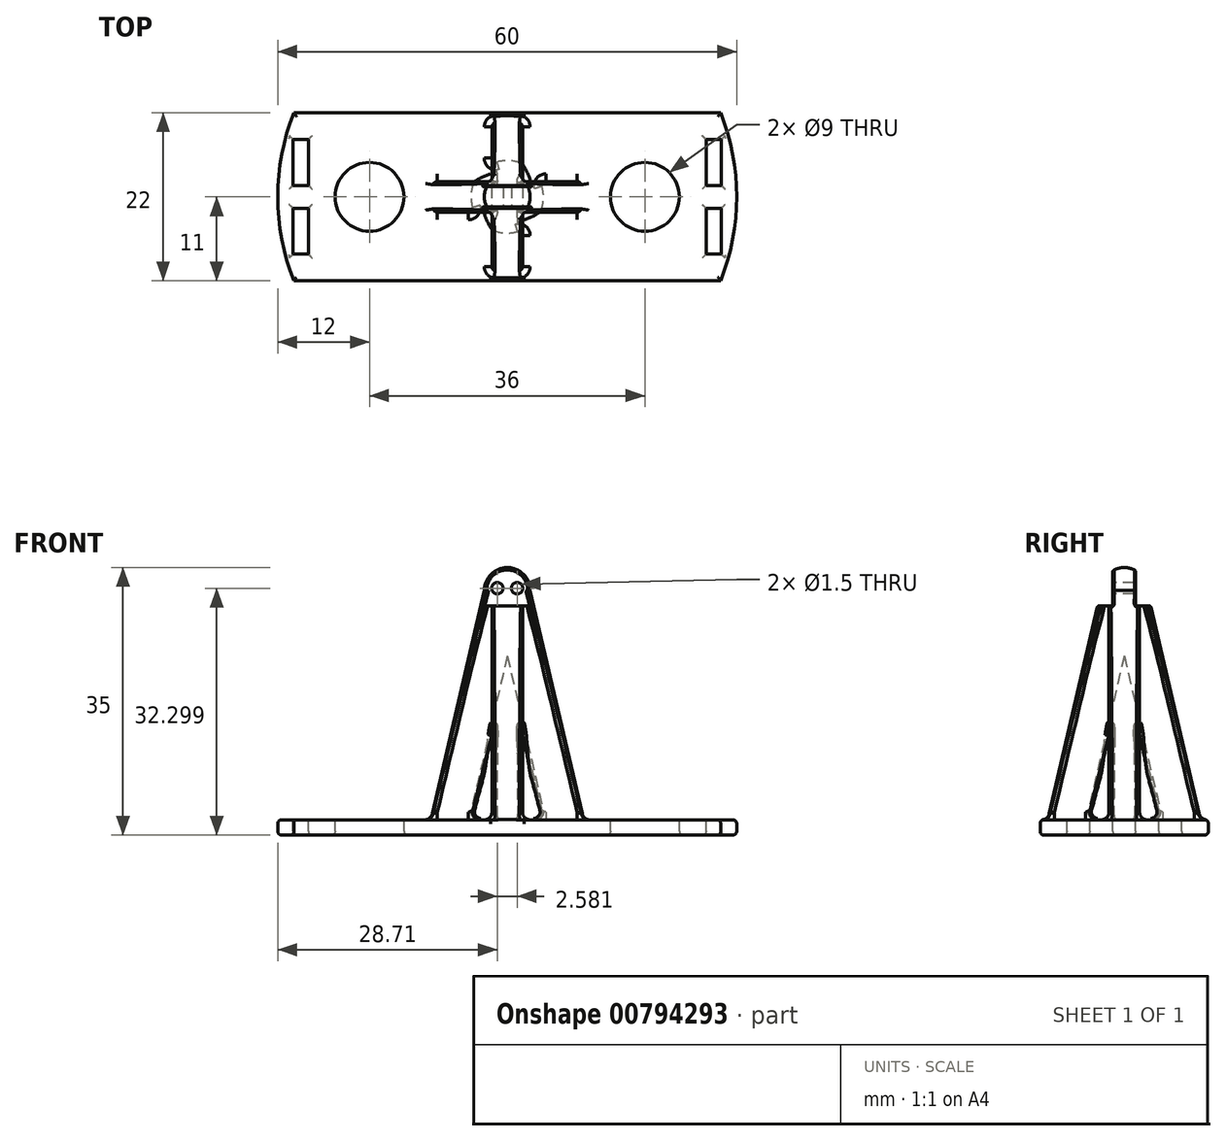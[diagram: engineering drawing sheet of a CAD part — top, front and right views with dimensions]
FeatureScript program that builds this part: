
annotation { "Feature Type Name" : "Feature", "Feature Type Description" : "" }
export const myFeature = defineFeature(function(context is Context, id is Id, definition is map)
    precondition{}
    {
        {
            var Q0;
            Q0=qCreatedBy(makeId("Front.planeOp"),FACE);
            var sketch = newSketch(context, id + "F0", { "sketchPlane" : qUnion([Q0])});
            skLineSegment(sketch, "E0", {"start": v(0, 0) * mm, "end": v(30, 0) * mm});
            skLineSegment(sketch, "E1", {"start": v(30, 0) * mm, "end": v(30, 2) * mm});
            skLineSegment(sketch, "E2", {"start": v(30, 2) * mm, "end": v(10, 2) * mm});
            skLineSegment(sketch, "E3", {"start": v(10, 2) * mm, "end": v(3, 32) * mm});
            skArc(sketch, "E4", {"start": v(3, 32) * mm, "mid": v(2.12, 34.12) * mm, "end": v(0, 35) * mm});
            skLineSegment(sketch, "E5", {"start": v(0, 32) * mm, "end": v(0, 35) * mm});
            skLineSegment(sketch, "E6", {"start": v(0, 2) * mm, "end": v(5, 2) * mm});
            skLineSegment(sketch, "E7", {"start": v(5, 2) * mm, "end": v(0, 23.43) * mm});
            skLineSegment(sketch, "E8", {"start": v(0, 32) * mm, "end": v(0, 23.43) * mm});
            skLineSegment(sketch, "E9", {"start": v(0, 2) * mm, "end": v(0, 0) * mm});
            skSolve(sketch);
        }
        {
            var Q0;
            Q0=makeQuery(id+"F0.imprint","IMPRINT",FACE,{"disambiguationData":[TD([[makeQuery(id+"F0.imprint","IMPRINT",EDGE,{"derivedFrom":sQuery(id+"F0.wireOp",EDGE,"E0")}),1.0]])]});
            var Q1;
            Q1=sQuery(id+"F0.wireOp",EDGE,"E8");
            revolve(context, id + "F1", {"surfaceOperationType" : NewSurfaceOperationType.NEW, "entities" : qUnion([Q0]), "axis" : qUnion([Q1]), "revolveType" : RevolveType.FULL});
        }
        {
            var Q0;
            Q0=makeQuery(id+"F1.opRevolve","SWEPT_FACE",FACE,{"disambiguationData":[OSD([sQuery(id+"F0.wireOp",EDGE,"E0")])]});
            var sketch = newSketch(context, id + "F2", { "sketchPlane" : qUnion([Q0])});
            skLineSegment(sketch, "E10.bottom", {"start": v(38.46, -11) * mm, "end": v(-38.46, -11) * mm});
            skLineSegment(sketch, "E10.top", {"start": v(38.46, 11) * mm, "end": v(-38.46, 11) * mm});
            skLineSegment(sketch, "E10.left", {"start": v(38.46, -11) * mm, "end": v(38.46, 11) * mm});
            skLineSegment(sketch, "E10.right", {"start": v(-38.46, -11) * mm, "end": v(-38.46, 11) * mm});
            skPoint(sketch, "E10.middle", {"position": v(0, 0) * mm});
            skSolve(sketch);
        }
        {
            var Q0;
            Q0 = qSketchRegion(id + "F2", true);
            extrude(context, id + "F3", {"entities" : qUnion([Q0]), "operationType" : NewBodyOperationType.INTERSECT, "endBound" : BoundingType.THROUGH_ALL, "oppositeDirection" : true, "depth" : 25 * mm, "offsetDistance" : 25 * mm});
        }
        {
            var Q0;
            Q0=makeQuery(id+"F3.boolean.opBoolean","SPLIT",FACE,{"disambiguationData":[OD(0.0)],"derivedFrom":makeQuery(id+"F1.opRevolve","SWEPT_FACE",FACE,{"disambiguationData":[OSD([sQuery(id+"F0.wireOp",EDGE,"E2")])]})});
            var sketch = newSketch(context, id + "F4", { "sketchPlane" : qUnion([Q0])});
            skLineSegment(sketch, "E11.bottom", {"start": v(-2, 2) * mm, "end": v(-12, 2) * mm});
            skLineSegment(sketch, "E11.top", {"start": v(-2, 12) * mm, "end": v(-12, 12) * mm});
            skLineSegment(sketch, "E11.left", {"start": v(-2, 2) * mm, "end": v(-2, 12) * mm});
            skLineSegment(sketch, "E11.right", {"start": v(-12, 2) * mm, "end": v(-12, 12) * mm});
            skLineSegment(sketch, "E12.1.0", {"start": v(-2, -2) * mm, "end": v(-2, -12) * mm});
            skLineSegment(sketch, "E12.1.1", {"start": v(-2, -2) * mm, "end": v(-12, -2) * mm});
            skLineSegment(sketch, "E12.1.2", {"start": v(-12, -2) * mm, "end": v(-12, -12) * mm});
            skLineSegment(sketch, "E12.1.3", {"start": v(-2, -12) * mm, "end": v(-12, -12) * mm});
            skLineSegment(sketch, "E12.2.0", {"start": v(2, -2) * mm, "end": v(12, -2) * mm});
            skLineSegment(sketch, "E12.2.1", {"start": v(2, -2) * mm, "end": v(2, -12) * mm});
            skLineSegment(sketch, "E12.2.2", {"start": v(2, -12) * mm, "end": v(12, -12) * mm});
            skLineSegment(sketch, "E12.2.3", {"start": v(12, -2) * mm, "end": v(12, -12) * mm});
            skLineSegment(sketch, "E12.3.0", {"start": v(2, 2) * mm, "end": v(2, 12) * mm});
            skLineSegment(sketch, "E12.3.1", {"start": v(2, 2) * mm, "end": v(12, 2) * mm});
            skLineSegment(sketch, "E12.3.2", {"start": v(12, 2) * mm, "end": v(12, 12) * mm});
            skLineSegment(sketch, "E12.3.3", {"start": v(2, 12) * mm, "end": v(12, 12) * mm});
            skPoint(sketch, "E12.center", {"position": v(0, 0) * mm});
            skSolve(sketch);
        }
        {
            var Q0;
            Q0 = qSketchRegion(id + "F4", true);
            extrude(context, id + "F5", {"entities" : qUnion([Q0]), "operationType" : NewBodyOperationType.REMOVE, "endBound" : BoundingType.THROUGH_ALL, "depth" : 25 * mm, "offsetDistance" : 25 * mm});
        }
        {
            var Q0;
            {var subQ0=makeQuery(id+"F1.opRevolve","SWEPT_FACE",FACE,{"disambiguationData":[OSD([sQuery(id+"F0.wireOp",EDGE,"E2")])]});Q0=makeQuery(id+"F5.boolean.opBoolean","MERGE",FACE,{"derivedFrom":[makeQuery(id+"F1.opRevolve","SWEPT_FACE",FACE,{"disambiguationData":[OSD([sQuery(id+"F0.wireOp",EDGE,"E6")])]}),makeQuery(id+"F3.boolean.opBoolean","SPLIT",FACE,{"disambiguationData":[OD(0.0)],"derivedFrom":subQ0}),makeQuery(id+"F3.boolean.opBoolean","SPLIT",FACE,{"disambiguationData":[OD(1.0)],"derivedFrom":subQ0}),makeQuery(id+"F5.opExtrude","CAP_FACE",FACE,{"disambiguationData":[OSD([sQuery(id+"F4.wireOp",EDGE,"E11.bottom"),sQuery(id+"F4.wireOp",EDGE,"E11.top"),sQuery(id+"F4.wireOp",EDGE,"E11.left"),sQuery(id+"F4.wireOp",EDGE,"E11.right")])],"isStart":true}),makeQuery(id+"F5.opExtrude","CAP_FACE",FACE,{"disambiguationData":[OSD([sQuery(id+"F4.wireOp",EDGE,"E12.1.0"),sQuery(id+"F4.wireOp",EDGE,"E12.1.1"),sQuery(id+"F4.wireOp",EDGE,"E12.1.2"),sQuery(id+"F4.wireOp",EDGE,"E12.1.3")])],"isStart":true}),makeQuery(id+"F5.opExtrude","CAP_FACE",FACE,{"disambiguationData":[OSD([sQuery(id+"F4.wireOp",EDGE,"E12.2.0"),sQuery(id+"F4.wireOp",EDGE,"E12.2.1"),sQuery(id+"F4.wireOp",EDGE,"E12.2.2"),sQuery(id+"F4.wireOp",EDGE,"E12.2.3")])],"isStart":true}),makeQuery(id+"F5.opExtrude","CAP_FACE",FACE,{"disambiguationData":[OSD([sQuery(id+"F4.wireOp",EDGE,"E12.3.0"),sQuery(id+"F4.wireOp",EDGE,"E12.3.1"),sQuery(id+"F4.wireOp",EDGE,"E12.3.2"),sQuery(id+"F4.wireOp",EDGE,"E12.3.3")])],"isStart":true})]});}
            cPlane(context, id + "F6", {"entities" : qUnion([Q0]), "cplaneType" : CPlaneType.OFFSET, "offset" : 33 * mm, "width" : 150 * mm, "height" : 150 * mm});
        }
        {
            var Q0;
            Q0=qCreatedBy(id+"F6.planeOp",FACE);
            var sketch = newSketch(context, id + "F7", { "sketchPlane" : qUnion([Q0])});
            skLineSegment(sketch, "E13.bottom", {"start": v(5, 1.5) * mm, "end": v(-5, 1.5) * mm, "construction": true});
            skLineSegment(sketch, "E13.top", {"start": v(5, -1.5) * mm, "end": v(-5, -1.5) * mm, "construction": true});
            skLineSegment(sketch, "E13.left", {"start": v(5, 1.5) * mm, "end": v(5, -1.5) * mm, "construction": true});
            skLineSegment(sketch, "E13.right", {"start": v(-5, 1.5) * mm, "end": v(-5, -1.5) * mm, "construction": true});
            skPoint(sketch, "E13.middle", {"position": v(0, 0) * mm});
            skLineSegment(sketch, "E14.bottom", {"start": v(-5, 1.5) * mm, "end": v(5, 1.5) * mm});
            skLineSegment(sketch, "E14.top", {"start": v(-5, 6.5) * mm, "end": v(5, 6.5) * mm});
            skLineSegment(sketch, "E14.left", {"start": v(-5, 1.5) * mm, "end": v(-5, 6.5) * mm});
            skLineSegment(sketch, "E14.right", {"start": v(5, 1.5) * mm, "end": v(5, 6.5) * mm});
            skLineSegment(sketch, "E15.bottom", {"start": v(-5, -1.5) * mm, "end": v(5, -1.5) * mm});
            skLineSegment(sketch, "E15.top", {"start": v(-5, -6.5) * mm, "end": v(5, -6.5) * mm});
            skLineSegment(sketch, "E15.left", {"start": v(-5, -1.5) * mm, "end": v(-5, -6.5) * mm});
            skLineSegment(sketch, "E15.right", {"start": v(5, -1.5) * mm, "end": v(5, -6.5) * mm});
            skSolve(sketch);
        }
        {
            var Q0;
            Q0 = qSketchRegion(id + "F7", true);
            extrude(context, id + "F8", {"entities" : qUnion([Q0]), "operationType" : NewBodyOperationType.REMOVE, "oppositeDirection" : true, "depth" : 5 * mm, "offsetDistance" : 25 * mm});
        }
        {
            var Q0;
            {var subQ0=makeQuery(id+"F1.opRevolve","SWEPT_FACE",FACE,{"disambiguationData":[OSD([sQuery(id+"F0.wireOp",EDGE,"E2")])]});Q0=makeQuery(id+"F5.boolean.opBoolean","MERGE",FACE,{"derivedFrom":[makeQuery(id+"F1.opRevolve","SWEPT_FACE",FACE,{"disambiguationData":[OSD([sQuery(id+"F0.wireOp",EDGE,"E6")])]}),makeQuery(id+"F3.boolean.opBoolean","SPLIT",FACE,{"disambiguationData":[OD(0.0)],"derivedFrom":subQ0}),makeQuery(id+"F3.boolean.opBoolean","SPLIT",FACE,{"disambiguationData":[OD(1.0)],"derivedFrom":subQ0}),makeQuery(id+"F5.opExtrude","CAP_FACE",FACE,{"disambiguationData":[OSD([sQuery(id+"F4.wireOp",EDGE,"E11.bottom"),sQuery(id+"F4.wireOp",EDGE,"E11.top"),sQuery(id+"F4.wireOp",EDGE,"E11.left"),sQuery(id+"F4.wireOp",EDGE,"E11.right")])],"isStart":true}),makeQuery(id+"F5.opExtrude","CAP_FACE",FACE,{"disambiguationData":[OSD([sQuery(id+"F4.wireOp",EDGE,"E12.1.0"),sQuery(id+"F4.wireOp",EDGE,"E12.1.1"),sQuery(id+"F4.wireOp",EDGE,"E12.1.2"),sQuery(id+"F4.wireOp",EDGE,"E12.1.3")])],"isStart":true}),makeQuery(id+"F5.opExtrude","CAP_FACE",FACE,{"disambiguationData":[OSD([sQuery(id+"F4.wireOp",EDGE,"E12.2.0"),sQuery(id+"F4.wireOp",EDGE,"E12.2.1"),sQuery(id+"F4.wireOp",EDGE,"E12.2.2"),sQuery(id+"F4.wireOp",EDGE,"E12.2.3")])],"isStart":true}),makeQuery(id+"F5.opExtrude","CAP_FACE",FACE,{"disambiguationData":[OSD([sQuery(id+"F4.wireOp",EDGE,"E12.3.0"),sQuery(id+"F4.wireOp",EDGE,"E12.3.1"),sQuery(id+"F4.wireOp",EDGE,"E12.3.2"),sQuery(id+"F4.wireOp",EDGE,"E12.3.3")])],"isStart":true})]});}
            var sketch = newSketch(context, id + "F9", { "sketchPlane" : qUnion([Q0])});
            skLineSegment(sketch, "E16", {"start": v(0, 0) * mm, "end": v(0, 11) * mm, "construction": true});
            skLineSegment(sketch, "E17", {"start": v(0, 0) * mm, "end": v(-30, 0) * mm, "construction": true});
            skLineSegment(sketch, "E18.bottom", {"start": v(-26, 1.5) * mm, "end": v(-28, 1.5) * mm});
            skLineSegment(sketch, "E18.top", {"start": v(-26, 7.5) * mm, "end": v(-28, 7.5) * mm});
            skLineSegment(sketch, "E18.left", {"start": v(-26, 1.5) * mm, "end": v(-26, 7.5) * mm});
            skLineSegment(sketch, "E18.right", {"start": v(-28, 1.5) * mm, "end": v(-28, 7.5) * mm});
            skLineSegment(sketch, "E19.MirrorCS", {"start": v(26, 1.5) * mm, "end": v(28, 1.5) * mm});
            skLineSegment(sketch, "E20.MirrorCS", {"start": v(26, 7.5) * mm, "end": v(28, 7.5) * mm});
            skLineSegment(sketch, "E21.MirrorCS", {"start": v(28, 1.5) * mm, "end": v(28, 7.5) * mm});
            skLineSegment(sketch, "E22.MirrorCS", {"start": v(26, 1.5) * mm, "end": v(26, 7.5) * mm});
            skLineSegment(sketch, "E23.MirrorCS", {"start": v(26, -7.5) * mm, "end": v(28, -7.5) * mm});
            skLineSegment(sketch, "E24.MirrorCS", {"start": v(28, -1.5) * mm, "end": v(28, -7.5) * mm});
            skLineSegment(sketch, "E25.MirrorCS", {"start": v(26, -1.5) * mm, "end": v(26, -7.5) * mm});
            skLineSegment(sketch, "E26.MirrorCS", {"start": v(26, -1.5) * mm, "end": v(28, -1.5) * mm});
            skLineSegment(sketch, "E27.MirrorCS", {"start": v(-28, -1.5) * mm, "end": v(-28, -7.5) * mm});
            skLineSegment(sketch, "E28.MirrorCS", {"start": v(-26, -1.5) * mm, "end": v(-26, -7.5) * mm});
            skLineSegment(sketch, "E29.MirrorCS", {"start": v(-26, -7.5) * mm, "end": v(-28, -7.5) * mm});
            skLineSegment(sketch, "E30.MirrorCS", {"start": v(-26, -1.5) * mm, "end": v(-28, -1.5) * mm});
            skSolve(sketch);
        }
        {
            var Q0;
            Q0 = qSketchRegion(id + "F9", true);
            extrude(context, id + "F10", {"entities" : qUnion([Q0]), "operationType" : NewBodyOperationType.REMOVE, "endBound" : BoundingType.UP_TO_NEXT, "oppositeDirection" : true, "depth" : 25 * mm, "offsetDistance" : 25 * mm});
        }
        {
            var Q0;
            Q0=makeQuery(id+"F8.boolean.opBoolean","COPY",FACE,{"derivedFrom":makeQuery(id+"F8.opExtrude","SWEPT_FACE",FACE,{"disambiguationData":[OSD([sQuery(id+"F7.wireOp",EDGE,"E15.bottom")])]})});
            var sketch = newSketch(context, id + "F11", { "sketchPlane" : qUnion([Q0])});
            skLineSegment(sketch, "E31", {"start": v(0, 34.6) * mm, "end": v(0, 30) * mm, "construction": true});
            skCircle(sketch, "E32", {"center": v(-1.3, 32.3) * mm, "radius": 0.75 * mm});
            skPoint(sketch, "E33", {"position": v(0, 32.3) * mm});
            skCircle(sketch, "E34.MirrorC", {"center": v(1.3, 32.3) * mm, "radius": 0.75 * mm});
            skLineSegment(sketch, "E35", {"start": v(0, 32.3) * mm, "end": v(-2.58, 32.3) * mm, "construction": true});
            skSolve(sketch);
        }
        {
            var Q0;
            Q0 = qSketchRegion(id + "F11", true);
            extrude(context, id + "F12", {"entities" : qUnion([Q0]), "operationType" : NewBodyOperationType.REMOVE, "endBound" : BoundingType.UP_TO_NEXT, "oppositeDirection" : true, "depth" : 25 * mm, "offsetDistance" : 25 * mm});
        }
        {
            var Q0;
            Q0=makeQuery(id+"F5.boolean.opBoolean","MERGE",FACE,{"derivedFrom":[makeQuery(id+"F1.opRevolve","SWEPT_FACE",FACE,{"disambiguationData":[OSD([sQuery(id+"F0.wireOp",EDGE,"E6")])]}),makeQuery(id+"F1.opRevolve","SWEPT_FACE",FACE,{"disambiguationData":[OSD([sQuery(id+"F0.wireOp",EDGE,"E2")])]}),makeQuery(id+"F5.opExtrude","CAP_FACE",FACE,{"disambiguationData":[OSD([sQuery(id+"F4.wireOp",EDGE,"E11.bottom"),sQuery(id+"F4.wireOp",EDGE,"E11.top"),sQuery(id+"F4.wireOp",EDGE,"E11.left"),sQuery(id+"F4.wireOp",EDGE,"E11.right")])],"isStart":true}),makeQuery(id+"F5.opExtrude","CAP_FACE",FACE,{"disambiguationData":[OSD([sQuery(id+"F4.wireOp",EDGE,"E12.1.0"),sQuery(id+"F4.wireOp",EDGE,"E12.1.1"),sQuery(id+"F4.wireOp",EDGE,"E12.1.2"),sQuery(id+"F4.wireOp",EDGE,"E12.1.3")])],"isStart":true}),makeQuery(id+"F5.opExtrude","CAP_FACE",FACE,{"disambiguationData":[OSD([sQuery(id+"F4.wireOp",EDGE,"E12.2.0"),sQuery(id+"F4.wireOp",EDGE,"E12.2.1"),sQuery(id+"F4.wireOp",EDGE,"E12.2.2"),sQuery(id+"F4.wireOp",EDGE,"E12.2.3")])],"isStart":true}),makeQuery(id+"F5.opExtrude","CAP_FACE",FACE,{"disambiguationData":[OSD([sQuery(id+"F4.wireOp",EDGE,"E12.3.0"),sQuery(id+"F4.wireOp",EDGE,"E12.3.1"),sQuery(id+"F4.wireOp",EDGE,"E12.3.2"),sQuery(id+"F4.wireOp",EDGE,"E12.3.3")])],"isStart":true})]});
            var sketch = newSketch(context, id + "F13", { "sketchPlane" : qUnion([Q0])});
            skCircle(sketch, "E36", {"center": v(-18, 0) * mm, "radius": 4.5 * mm});
            skLineSegment(sketch, "E37", {"start": v(0, 0) * mm, "end": v(0, 11) * mm, "construction": true});
            skCircle(sketch, "E38.MirrorC", {"center": v(18, 0) * mm, "radius": 4.5 * mm});
            skLineSegment(sketch, "E39", {"start": v(-10, 0) * mm, "end": v(-26, 0) * mm, "construction": true});
            skSolve(sketch);
        }
        {
            var Q0;
            Q0 = qSketchRegion(id + "F13", true);
            extrude(context, id + "F14", {"entities" : qUnion([Q0]), "operationType" : NewBodyOperationType.REMOVE, "endBound" : BoundingType.UP_TO_NEXT, "oppositeDirection" : true, "depth" : 25 * mm, "offsetDistance" : 25 * mm});
        }
        {
            var Q0;
            Q0=makeQuery(id+"F12.boolean.opBoolean","COPY",FACE,{"derivedFrom":makeQuery(id+"F12.opExtrude","SWEPT_FACE",FACE,{"disambiguationData":[OSD([sQuery(id+"F11.wireOp",EDGE,"E32")])]})});
            var Q1;
            Q1=makeQuery(id+"F12.boolean.opBoolean","COPY",FACE,{"derivedFrom":makeQuery(id+"F12.opExtrude","SWEPT_FACE",FACE,{"disambiguationData":[OSD([sQuery(id+"F11.wireOp",EDGE,"E34.MirrorC")])]})});
            var Q2;
            Q2=makeQuery(id+"F8.boolean.opBoolean","COPY",EDGE,{"derivedFrom":makeQuery(id+"F8.opExtrude","CAP_EDGE",EDGE,{"disambiguationData":[OSD([sQuery(id+"F7.wireOp",EDGE,"E14.bottom")])],"isStart":false})});
            var Q3;
            Q3=makeQuery(id+"F8.boolean.opBoolean","COPY",EDGE,{"derivedFrom":makeQuery(id+"F8.opExtrude","CAP_EDGE",EDGE,{"disambiguationData":[OSD([sQuery(id+"F7.wireOp",EDGE,"E15.bottom")])],"isStart":false})});
            fillet(context, id + "F15", {"entities" : qUnion([Q0, Q1, Q2, Q3]), "radius" : 0.2 * mm, "tangentPropagation" : true, "allowEdgeOverflow" : false});
        }
        {
            var Q0;
            Q0=makeQuery(id+"F5.boolean.opBoolean","INTERSECT",EDGE,{"derivedFrom":[makeQuery(id+"F1.opRevolve","SWEPT_FACE",FACE,{"disambiguationData":[OSD([sQuery(id+"F0.wireOp",EDGE,"E3")])]}),makeQuery(id+"F5.opExtrude","SWEPT_FACE",FACE,{"disambiguationData":[OSD([sQuery(id+"F4.wireOp",EDGE,"E12.3.0")])]})]});
            var Q1;
            Q1=makeQuery(id+"F5.boolean.opBoolean","COPY",EDGE,{"derivedFrom":makeQuery(id+"F5.opExtrude","SWEPT_EDGE",EDGE,{"disambiguationData":[OSD([sQuery(id+"F4.wireOp",EDGE,"E12.3.0"),sQuery(id+"F4.wireOp",EDGE,"E12.3.1")])]})});
            var Q2;
            Q2=makeQuery(id+"F5.boolean.opBoolean","INTERSECT",EDGE,{"derivedFrom":[makeQuery(id+"F1.opRevolve","SWEPT_FACE",FACE,{"disambiguationData":[OSD([sQuery(id+"F0.wireOp",EDGE,"E3")])]}),makeQuery(id+"F5.opExtrude","SWEPT_FACE",FACE,{"disambiguationData":[OSD([sQuery(id+"F4.wireOp",EDGE,"E12.3.1")])]})]});
            var Q3;
            Q3=makeQuery(id+"F5.boolean.opBoolean","INTERSECT",EDGE,{"derivedFrom":[makeQuery(id+"F1.opRevolve","SWEPT_FACE",FACE,{"disambiguationData":[OSD([sQuery(id+"F0.wireOp",EDGE,"E3")])]}),makeQuery(id+"F5.opExtrude","SWEPT_FACE",FACE,{"disambiguationData":[OSD([sQuery(id+"F4.wireOp",EDGE,"E12.2.0")])]})]});
            var Q4;
            Q4=makeQuery(id+"F5.boolean.opBoolean","COPY",EDGE,{"derivedFrom":makeQuery(id+"F5.opExtrude","SWEPT_EDGE",EDGE,{"disambiguationData":[OSD([sQuery(id+"F4.wireOp",EDGE,"E12.2.0"),sQuery(id+"F4.wireOp",EDGE,"E12.2.1")])]})});
            var Q5;
            Q5=makeQuery(id+"F5.boolean.opBoolean","INTERSECT",EDGE,{"derivedFrom":[makeQuery(id+"F1.opRevolve","SWEPT_FACE",FACE,{"disambiguationData":[OSD([sQuery(id+"F0.wireOp",EDGE,"E3")])]}),makeQuery(id+"F5.opExtrude","SWEPT_FACE",FACE,{"disambiguationData":[OSD([sQuery(id+"F4.wireOp",EDGE,"E12.2.1")])]})]});
            var Q6;
            Q6=makeQuery(id+"F5.boolean.opBoolean","INTERSECT",EDGE,{"derivedFrom":[makeQuery(id+"F1.opRevolve","SWEPT_FACE",FACE,{"disambiguationData":[OSD([sQuery(id+"F0.wireOp",EDGE,"E3")])]}),makeQuery(id+"F5.opExtrude","SWEPT_FACE",FACE,{"disambiguationData":[OSD([sQuery(id+"F4.wireOp",EDGE,"E12.1.0")])]})]});
            var Q7;
            Q7=makeQuery(id+"F5.boolean.opBoolean","COPY",EDGE,{"derivedFrom":makeQuery(id+"F5.opExtrude","SWEPT_EDGE",EDGE,{"disambiguationData":[OSD([sQuery(id+"F4.wireOp",EDGE,"E12.1.0"),sQuery(id+"F4.wireOp",EDGE,"E12.1.1")])]})});
            var Q8;
            Q8=makeQuery(id+"F5.boolean.opBoolean","INTERSECT",EDGE,{"derivedFrom":[makeQuery(id+"F1.opRevolve","SWEPT_FACE",FACE,{"disambiguationData":[OSD([sQuery(id+"F0.wireOp",EDGE,"E3")])]}),makeQuery(id+"F5.opExtrude","SWEPT_FACE",FACE,{"disambiguationData":[OSD([sQuery(id+"F4.wireOp",EDGE,"E12.1.1")])]})]});
            var Q9;
            Q9=makeQuery(id+"F5.boolean.opBoolean","INTERSECT",EDGE,{"derivedFrom":[makeQuery(id+"F1.opRevolve","SWEPT_FACE",FACE,{"disambiguationData":[OSD([sQuery(id+"F0.wireOp",EDGE,"E3")])]}),makeQuery(id+"F5.opExtrude","SWEPT_FACE",FACE,{"disambiguationData":[OSD([sQuery(id+"F4.wireOp",EDGE,"E11.bottom")])]})]});
            var Q10;
            Q10=makeQuery(id+"F5.boolean.opBoolean","COPY",EDGE,{"derivedFrom":makeQuery(id+"F5.opExtrude","SWEPT_EDGE",EDGE,{"disambiguationData":[OSD([sQuery(id+"F4.wireOp",EDGE,"E11.bottom"),sQuery(id+"F4.wireOp",EDGE,"E11.left")])]})});
            var Q11;
            Q11=makeQuery(id+"F5.boolean.opBoolean","INTERSECT",EDGE,{"derivedFrom":[makeQuery(id+"F1.opRevolve","SWEPT_FACE",FACE,{"disambiguationData":[OSD([sQuery(id+"F0.wireOp",EDGE,"E3")])]}),makeQuery(id+"F5.opExtrude","SWEPT_FACE",FACE,{"disambiguationData":[OSD([sQuery(id+"F4.wireOp",EDGE,"E11.left")])]})]});
            var Q12;
            Q12=makeQuery(id+"F5.boolean.opBoolean","INTERSECT",EDGE,{"derivedFrom":[makeQuery(id+"F1.opRevolve","SWEPT_FACE",FACE,{"disambiguationData":[OSD([sQuery(id+"F0.wireOp",EDGE,"E7")])]}),makeQuery(id+"F5.opExtrude","SWEPT_FACE",FACE,{"disambiguationData":[OSD([sQuery(id+"F4.wireOp",EDGE,"E12.3.1")])]})]});
            var Q13;
            Q13=makeQuery(id+"F5.boolean.opBoolean","INTERSECT",EDGE,{"derivedFrom":[makeQuery(id+"F1.opRevolve","SWEPT_FACE",FACE,{"disambiguationData":[OSD([sQuery(id+"F0.wireOp",EDGE,"E7")])]}),makeQuery(id+"F5.opExtrude","SWEPT_FACE",FACE,{"disambiguationData":[OSD([sQuery(id+"F4.wireOp",EDGE,"E11.left")])]})]});
            var Q14;
            Q14=makeQuery(id+"F5.boolean.opBoolean","INTERSECT",EDGE,{"derivedFrom":[makeQuery(id+"F1.opRevolve","SWEPT_FACE",FACE,{"disambiguationData":[OSD([sQuery(id+"F0.wireOp",EDGE,"E7")])]}),makeQuery(id+"F5.opExtrude","SWEPT_FACE",FACE,{"disambiguationData":[OSD([sQuery(id+"F4.wireOp",EDGE,"E12.1.1")])]})]});
            var Q15;
            Q15=makeQuery(id+"F5.boolean.opBoolean","INTERSECT",EDGE,{"derivedFrom":[makeQuery(id+"F1.opRevolve","SWEPT_FACE",FACE,{"disambiguationData":[OSD([sQuery(id+"F0.wireOp",EDGE,"E7")])]}),makeQuery(id+"F5.opExtrude","SWEPT_FACE",FACE,{"disambiguationData":[OSD([sQuery(id+"F4.wireOp",EDGE,"E12.2.1")])]})]});
            fillet(context, id + "F16", {"entities" : qUnion([Q0, Q1, Q2, Q3, Q4, Q5, Q6, Q7, Q8, Q9, Q10, Q11, Q12, Q13, Q14, Q15]), "radius" : 0.5 * mm, "tangentPropagation" : true, "allowEdgeOverflow" : false});
        }
        {
            var Q0;
            Q0=makeQuery(id+"F5.boolean.opBoolean","COPY",EDGE,{"derivedFrom":makeQuery(id+"F5.opExtrude","CAP_EDGE",EDGE,{"disambiguationData":[OSD([sQuery(id+"F4.wireOp",EDGE,"E12.3.1")])],"isStart":true})});
            var Q1;
            Q1=makeQuery(id+"F5.boolean.opBoolean","COPY",EDGE,{"derivedFrom":makeQuery(id+"F5.opExtrude","CAP_EDGE",EDGE,{"disambiguationData":[OSD([sQuery(id+"F4.wireOp",EDGE,"E11.bottom")])],"isStart":true})});
            var Q2;
            Q2=makeQuery(id+"F5.boolean.opBoolean","COPY",EDGE,{"derivedFrom":makeQuery(id+"F5.opExtrude","CAP_EDGE",EDGE,{"disambiguationData":[OSD([sQuery(id+"F4.wireOp",EDGE,"E12.2.1")])],"isStart":true})});
            var Q3;
            Q3=makeQuery(id+"F5.boolean.opBoolean","COPY",EDGE,{"derivedFrom":makeQuery(id+"F5.opExtrude","CAP_EDGE",EDGE,{"disambiguationData":[OSD([sQuery(id+"F4.wireOp",EDGE,"E11.left")])],"isStart":true})});
            fillet(context, id + "F17", {"entities" : qUnion([Q0, Q1, Q2, Q3]), "radius" : 1 * mm, "tangentPropagation" : true, "allowEdgeOverflow" : false});
        }
        {
            var Q0;
            Q0=makeQuery(id+"F10.boolean.opBoolean","COPY",EDGE,{"derivedFrom":makeQuery(id+"F10.opExtrude","CAP_EDGE",EDGE,{"disambiguationData":[OSD([sQuery(id+"F9.wireOp",EDGE,"E18.right")])],"isStart":true})});
            var Q1;
            Q1=makeQuery(id+"F10.boolean.opBoolean","COPY",EDGE,{"derivedFrom":makeQuery(id+"F10.opExtrude","CAP_EDGE",EDGE,{"disambiguationData":[OSD([sQuery(id+"F9.wireOp",EDGE,"E18.top")])],"isStart":true})});
            var Q2;
            Q2=makeQuery(id+"F10.boolean.opBoolean","COPY",EDGE,{"derivedFrom":makeQuery(id+"F10.opExtrude","CAP_EDGE",EDGE,{"disambiguationData":[OSD([sQuery(id+"F9.wireOp",EDGE,"E18.left")])],"isStart":true})});
            var Q3;
            Q3=makeQuery(id+"F10.boolean.opBoolean","COPY",EDGE,{"derivedFrom":makeQuery(id+"F10.opExtrude","CAP_EDGE",EDGE,{"disambiguationData":[OSD([sQuery(id+"F9.wireOp",EDGE,"E18.bottom")])],"isStart":true})});
            var Q4;
            Q4=makeQuery(id+"F10.boolean.opBoolean","COPY",EDGE,{"derivedFrom":makeQuery(id+"F10.opExtrude","CAP_EDGE",EDGE,{"disambiguationData":[OSD([sQuery(id+"F9.wireOp",EDGE,"E27.MirrorCS")])],"isStart":true})});
            var Q5;
            Q5=makeQuery(id+"F10.boolean.opBoolean","COPY",EDGE,{"derivedFrom":makeQuery(id+"F10.opExtrude","CAP_EDGE",EDGE,{"disambiguationData":[OSD([sQuery(id+"F9.wireOp",EDGE,"E30.MirrorCS")])],"isStart":true})});
            var Q6;
            Q6=makeQuery(id+"F10.boolean.opBoolean","COPY",EDGE,{"derivedFrom":makeQuery(id+"F10.opExtrude","CAP_EDGE",EDGE,{"disambiguationData":[OSD([sQuery(id+"F9.wireOp",EDGE,"E28.MirrorCS")])],"isStart":true})});
            var Q7;
            Q7=makeQuery(id+"F10.boolean.opBoolean","COPY",EDGE,{"derivedFrom":makeQuery(id+"F10.opExtrude","CAP_EDGE",EDGE,{"disambiguationData":[OSD([sQuery(id+"F9.wireOp",EDGE,"E29.MirrorCS")])],"isStart":true})});
            var Q8;
            Q8=makeQuery(id+"F10.boolean.opBoolean","COPY",EDGE,{"derivedFrom":makeQuery(id+"F10.opExtrude","CAP_EDGE",EDGE,{"disambiguationData":[OSD([sQuery(id+"F9.wireOp",EDGE,"E22.MirrorCS")])],"isStart":true})});
            var Q9;
            Q9=makeQuery(id+"F10.boolean.opBoolean","COPY",EDGE,{"derivedFrom":makeQuery(id+"F10.opExtrude","CAP_EDGE",EDGE,{"disambiguationData":[OSD([sQuery(id+"F9.wireOp",EDGE,"E20.MirrorCS")])],"isStart":true})});
            var Q10;
            Q10=makeQuery(id+"F10.boolean.opBoolean","COPY",EDGE,{"derivedFrom":makeQuery(id+"F10.opExtrude","CAP_EDGE",EDGE,{"disambiguationData":[OSD([sQuery(id+"F9.wireOp",EDGE,"E21.MirrorCS")])],"isStart":true})});
            var Q11;
            Q11=makeQuery(id+"F10.boolean.opBoolean","COPY",EDGE,{"derivedFrom":makeQuery(id+"F10.opExtrude","CAP_EDGE",EDGE,{"disambiguationData":[OSD([sQuery(id+"F9.wireOp",EDGE,"E19.MirrorCS")])],"isStart":true})});
            var Q12;
            Q12=makeQuery(id+"F10.boolean.opBoolean","COPY",EDGE,{"derivedFrom":makeQuery(id+"F10.opExtrude","CAP_EDGE",EDGE,{"disambiguationData":[OSD([sQuery(id+"F9.wireOp",EDGE,"E25.MirrorCS")])],"isStart":true})});
            var Q13;
            Q13=makeQuery(id+"F10.boolean.opBoolean","COPY",EDGE,{"derivedFrom":makeQuery(id+"F10.opExtrude","CAP_EDGE",EDGE,{"disambiguationData":[OSD([sQuery(id+"F9.wireOp",EDGE,"E26.MirrorCS")])],"isStart":true})});
            var Q14;
            Q14=makeQuery(id+"F10.boolean.opBoolean","COPY",EDGE,{"derivedFrom":makeQuery(id+"F10.opExtrude","CAP_EDGE",EDGE,{"disambiguationData":[OSD([sQuery(id+"F9.wireOp",EDGE,"E24.MirrorCS")])],"isStart":true})});
            var Q15;
            Q15=makeQuery(id+"F10.boolean.opBoolean","COPY",EDGE,{"derivedFrom":makeQuery(id+"F10.opExtrude","CAP_EDGE",EDGE,{"disambiguationData":[OSD([sQuery(id+"F9.wireOp",EDGE,"E23.MirrorCS")])],"isStart":true})});
            var Q16;
            Q16=makeQuery(id+"F5.boolean.opBoolean","INTERSECT",EDGE,{"derivedFrom":[makeQuery(id+"F5.opExtrude","CAP_FACE",FACE,{"disambiguationData":[OSD([sQuery(id+"F4.wireOp",EDGE,"E12.1.0"),sQuery(id+"F4.wireOp",EDGE,"E12.1.1"),sQuery(id+"F4.wireOp",EDGE,"E12.1.2"),sQuery(id+"F4.wireOp",EDGE,"E12.1.3")])],"isStart":true}),makeQuery(id+"F5.opExtrude","CAP_FACE",FACE,{"disambiguationData":[OSD([sQuery(id+"F4.wireOp",EDGE,"E12.2.0"),sQuery(id+"F4.wireOp",EDGE,"E12.2.1"),sQuery(id+"F4.wireOp",EDGE,"E12.2.2"),sQuery(id+"F4.wireOp",EDGE,"E12.2.3")])],"isStart":true})]});
            var Q17;
            Q17=makeQuery(id+"F3.boolean.opBoolean","SPLIT",EDGE,{"disambiguationData":[OD(1.0)],"derivedFrom":makeQuery(id+"F1.opRevolve","SWEPT_EDGE",EDGE,{"disambiguationData":[OSD([sQuery(id+"F0.wireOp",EDGE,"E1"),sQuery(id+"F0.wireOp",EDGE,"E2")])]})});
            var Q18;
            Q18=makeQuery(id+"F5.boolean.opBoolean","INTERSECT",EDGE,{"derivedFrom":[makeQuery(id+"F5.opExtrude","CAP_FACE",FACE,{"disambiguationData":[OSD([sQuery(id+"F4.wireOp",EDGE,"E11.bottom"),sQuery(id+"F4.wireOp",EDGE,"E11.top"),sQuery(id+"F4.wireOp",EDGE,"E11.left"),sQuery(id+"F4.wireOp",EDGE,"E11.right")])],"isStart":true}),makeQuery(id+"F5.opExtrude","CAP_FACE",FACE,{"disambiguationData":[OSD([sQuery(id+"F4.wireOp",EDGE,"E12.3.0"),sQuery(id+"F4.wireOp",EDGE,"E12.3.1"),sQuery(id+"F4.wireOp",EDGE,"E12.3.2"),sQuery(id+"F4.wireOp",EDGE,"E12.3.3")])],"isStart":true})]});
            var Q19;
            Q19=makeQuery(id+"F3.boolean.opBoolean","SPLIT",EDGE,{"disambiguationData":[OD(0.0)],"derivedFrom":makeQuery(id+"F1.opRevolve","SWEPT_EDGE",EDGE,{"disambiguationData":[OSD([sQuery(id+"F0.wireOp",EDGE,"E1"),sQuery(id+"F0.wireOp",EDGE,"E2")])]})});
            var Q20;
            Q20=makeQuery(id+"F14.boolean.opBoolean","COPY",EDGE,{"derivedFrom":makeQuery(id+"F14.opExtrude","CAP_EDGE",EDGE,{"disambiguationData":[OSD([sQuery(id+"F13.wireOp",EDGE,"E36")])],"isStart":true})});
            var Q21;
            Q21=makeQuery(id+"F14.boolean.opBoolean","COPY",EDGE,{"derivedFrom":makeQuery(id+"F14.opExtrude","CAP_EDGE",EDGE,{"disambiguationData":[OSD([sQuery(id+"F13.wireOp",EDGE,"E38.MirrorC")])],"isStart":true})});
            fillet(context, id + "F18", {"entities" : qUnion([Q0, Q1, Q2, Q3, Q4, Q5, Q6, Q7, Q8, Q9, Q10, Q11, Q12, Q13, Q14, Q15, Q16, Q17, Q18, Q19, Q20, Q21]), "radius" : 0.5 * mm, "tangentPropagation" : true, "allowEdgeOverflow" : false});
        }
        {
            var Q0;
            Q0=makeQuery(id+"F8.boolean.opBoolean","COPY",FACE,{"derivedFrom":makeQuery(id+"F8.opExtrude","SWEPT_FACE",FACE,{"disambiguationData":[OSD([sQuery(id+"F7.wireOp",EDGE,"E14.bottom")])]})});
            var Q1;
            Q1=makeQuery(id+"F8.boolean.opBoolean","COPY",FACE,{"derivedFrom":makeQuery(id+"F8.opExtrude","SWEPT_FACE",FACE,{"disambiguationData":[OSD([sQuery(id+"F7.wireOp",EDGE,"E15.bottom")])]})});
            fillet(context, id + "F19", {"entities" : qUnion([Q0, Q1]), "radius" : 0.3 * mm, "tangentPropagation" : true, "allowEdgeOverflow" : false});
        }
        {
            var Q0;
            Q0=makeQuery(id+"F1.opRevolve","SWEPT_FACE",FACE,{"disambiguationData":[OSD([sQuery(id+"F0.wireOp",EDGE,"E0")])]});
            fillet(context, id + "F20", {"entities" : qUnion([Q0]), "radius" : 0.5 * mm, "tangentPropagation" : true, "allowEdgeOverflow" : false});
        }
    });
